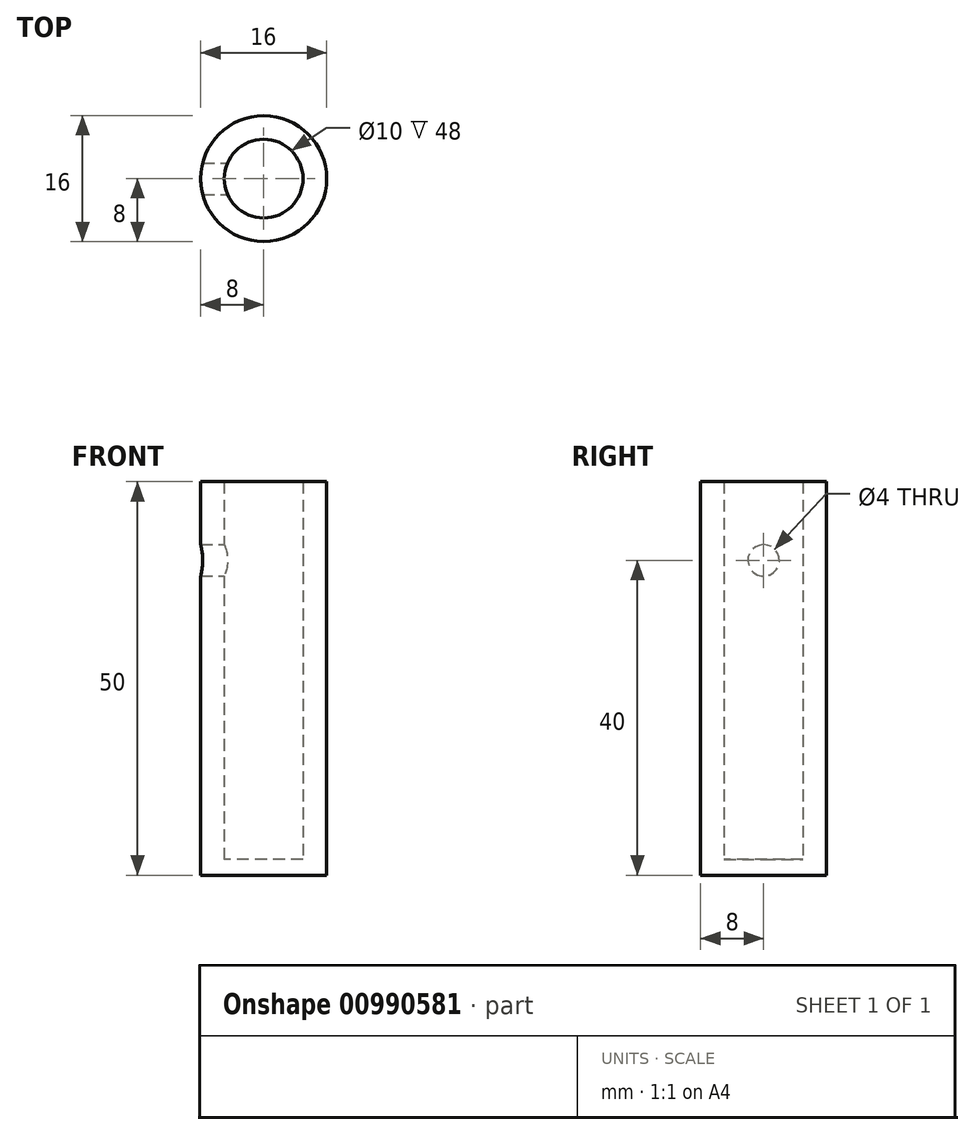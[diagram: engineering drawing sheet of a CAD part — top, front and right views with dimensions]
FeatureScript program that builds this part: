
annotation { "Feature Type Name" : "Feature", "Feature Type Description" : "" }
export const myFeature = defineFeature(function(context is Context, id is Id, definition is map)
    precondition{}
    {
        {
            var Q0;
            Q0=qCreatedBy(makeId("Top.planeOp"),FACE);
            var sketch = newSketch(context, id + "F0", { "sketchPlane" : qUnion([Q0])});
            skCircle(sketch, "E0", {"center": v(0, 0) * mm, "radius": 5 * mm});
            skCircle(sketch, "E1", {"center": v(0, 0) * mm, "radius": 8 * mm});
            skSolve(sketch);
        }
        {
            var Q0;
            Q0=makeQuery(id+"F0.imprint","IMPRINT",FACE,{"disambiguationData":[TD([[makeQuery(id+"F0.imprint","IMPRINT",EDGE,{"derivedFrom":sQuery(id+"F0.wireOp",EDGE,"E0")}),-1.0]])]});
            extrude(context, id + "F1", {"entities" : qUnion([Q0]), "depth" : 50 * mm, "offsetDistance" : 25 * mm});
        }
        {
            var Q0;
            Q0=makeQuery(id+"F0.imprint","IMPRINT",FACE,{"disambiguationData":[TD([[makeQuery(id+"F0.imprint","IMPRINT",EDGE,{"derivedFrom":sQuery(id+"F0.wireOp",EDGE,"E0")}),1.0]])]});
            extrude(context, id + "F2", {"entities" : qUnion([Q0]), "operationType" : NewBodyOperationType.ADD, "depth" : 2 * mm, "offsetDistance" : 25 * mm});
        }
        {
            var Q0;
            Q0=qCreatedBy(makeId("Right.planeOp"),FACE);
            var sketch = newSketch(context, id + "F3", { "sketchPlane" : qUnion([Q0])});
            skCircle(sketch, "E2", {"center": v(0, 40) * mm, "radius": 2 * mm});
            skSolve(sketch);
        }
        {
            var Q0;
            Q0 = qSketchRegion(id + "F3", true);
            extrude(context, id + "F4", {"entities" : qUnion([Q0]), "operationType" : NewBodyOperationType.REMOVE, "oppositeDirection" : true, "depth" : 25 * mm, "offsetDistance" : 25 * mm});
        }
    });
